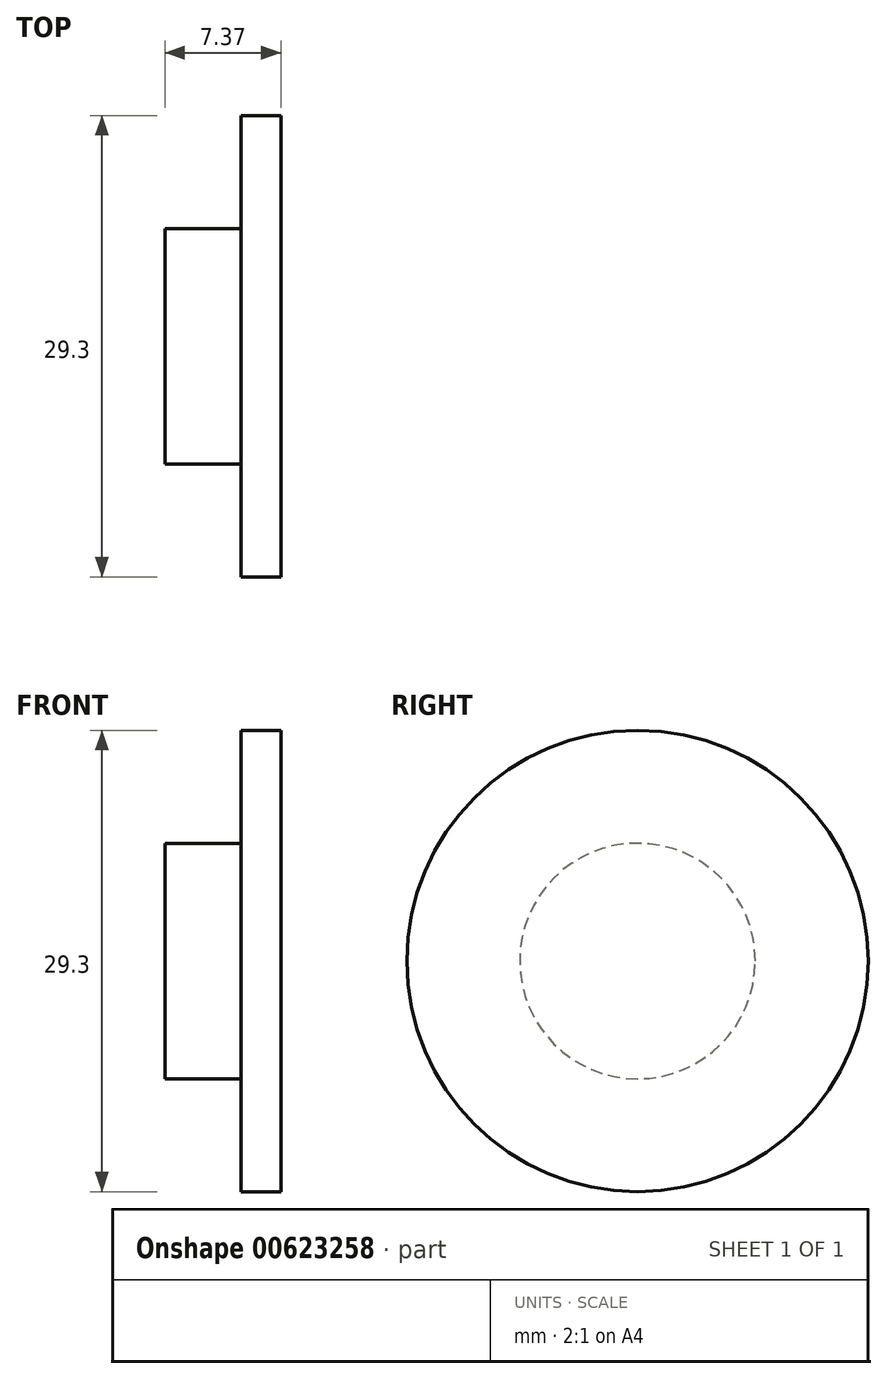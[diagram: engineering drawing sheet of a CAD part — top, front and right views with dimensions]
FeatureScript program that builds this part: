
annotation { "Feature Type Name" : "Feature", "Feature Type Description" : "" }
export const myFeature = defineFeature(function(context is Context, id is Id, definition is map)
    precondition{}
    {
        {
            var Q0;
            Q0=qCreatedBy(makeId("Right.planeOp"),FACE);
            var sketch = newSketch(context, id + "F0", { "sketchPlane" : qUnion([Q0])});
            skCircle(sketch, "E0", {"center": v(0, 0) * mm, "radius": 14.65 * mm});
            skSolve(sketch);
        }
        {
            var Q0;
            Q0=qSketchRegion(id+"F0",true);
            extrude(context, id + "F1", {"entities" : qUnion([Q0]), "depth" : 2.54 * mm, "offsetDistance" : 25.4 * mm});
        }
        {
            var Q0;
            Q0=qCreatedBy(makeId("Right.planeOp"),FACE);
            var sketch = newSketch(context, id + "F2", { "sketchPlane" : qUnion([Q0])});
            skCircle(sketch, "E1", {"center": v(0, 0) * mm, "radius": 7.48 * mm});
            skSolve(sketch);
        }
        {
            var Q0;
            Q0=qSketchRegion(id+"F2",true);
            extrude(context, id + "F3", {"entities" : qUnion([Q0]), "operationType" : NewBodyOperationType.ADD, "oppositeDirection" : true, "depth" : 4.83 * mm, "offsetDistance" : 25.4 * mm});
        }
    });
